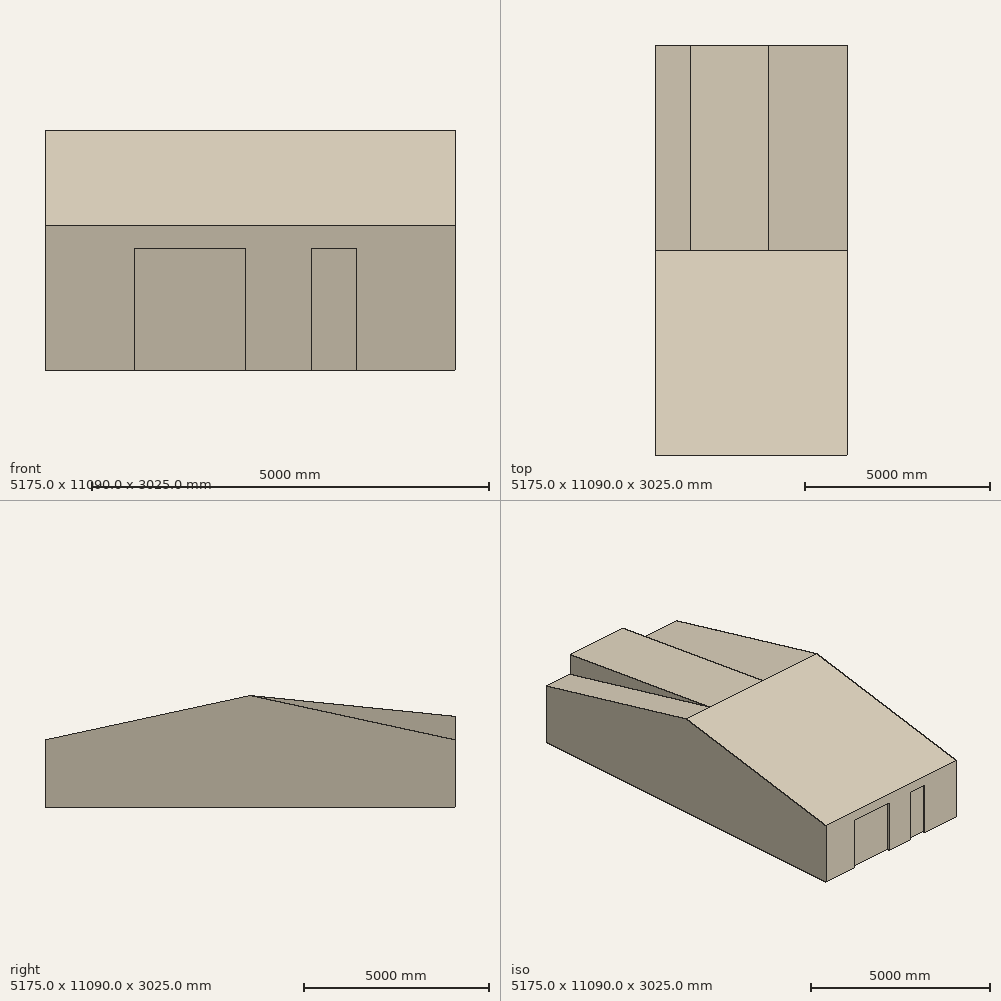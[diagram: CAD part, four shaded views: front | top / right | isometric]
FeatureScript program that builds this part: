
annotation { "Feature Type Name" : "Feature", "Feature Type Description" : "" }
export const myFeature = defineFeature(function(context is Context, id is Id, definition is map)
    precondition{}
    {
        {
            var Q0;
            Q0=qCreatedBy(makeId("Top.planeOp"),FACE);
            var sketch = newSketch(context, id + "F0", { "sketchPlane" : qUnion([Q0])});
            skLineSegment(sketch, "E0", {"start": v(0, 0) * mm, "end": v(5175, 0) * mm});
            skLineSegment(sketch, "E1", {"start": v(5175, 0) * mm, "end": v(5175, -11090) * mm});
            skLineSegment(sketch, "E2", {"start": v(5175, -11090) * mm, "end": v(0, -11090) * mm});
            skLineSegment(sketch, "E3", {"start": v(0, -11090) * mm, "end": v(0, 0) * mm});
            skSolve(sketch);
        }
        {
            var Q0;
            Q0 = qSketchRegion(id + "F0", true);
            extrude(context, id + "F1", {"entities" : qUnion([Q0]), "depth" : 3025 * mm, "offsetDistance" : 25 * mm});
        }
        {
            var Q0;
            Q0=makeQuery(id+"F1.opExtrude","SWEPT_FACE",FACE,{"disambiguationData":[OSD([sQuery(id+"F0.wireOp",EDGE,"E2")])]});
            var sketch = newSketch(context, id + "F2", { "sketchPlane" : qUnion([Q0])});
            skLineSegment(sketch, "E4", {"start": v(1120, 1540) * mm, "end": v(1120, 0) * mm});
            skLineSegment(sketch, "E5", {"start": v(1120, 1540) * mm, "end": v(2520, 1540) * mm});
            skLineSegment(sketch, "E6", {"start": v(2520, 1540) * mm, "end": v(2520, 0) * mm});
            skLineSegment(sketch, "E7", {"start": v(3360, 1540) * mm, "end": v(3360, 0) * mm});
            skLineSegment(sketch, "E8", {"start": v(3360, 1540) * mm, "end": v(3920, 1540) * mm});
            skLineSegment(sketch, "E9", {"start": v(3920, 1540) * mm, "end": v(3920, 0) * mm});
            skSolve(sketch);
        }
        {
            var Q0;
            Q0=makeQuery(id+"F1.opExtrude","SWEPT_FACE",FACE,{"disambiguationData":[OSD([sQuery(id+"F0.wireOp",EDGE,"E0")])]});
            var sketch = newSketch(context, id + "F3", { "sketchPlane" : qUnion([Q0])});
            skLineSegment(sketch, "E10", {"start": v(-2735, 1400) * mm, "end": v(-2735, 0) * mm});
            skLineSegment(sketch, "E11", {"start": v(-2735, 1400) * mm, "end": v(-1235, 1400) * mm});
            skLineSegment(sketch, "E12", {"start": v(-1235, 1400) * mm, "end": v(-1235, -91.11) * mm});
            skSolve(sketch);
        }
        {
            var Q0;
            Q0=makeQuery(id+"F1.opExtrude","SWEPT_FACE",FACE,{"disambiguationData":[OSD([sQuery(id+"F0.wireOp",EDGE,"E1")])]});
            var sketch = newSketch(context, id + "F4", { "sketchPlane" : qUnion([Q0])});
            skLineSegment(sketch, "E13", {"start": v(-5545, 3025) * mm, "end": v(-11090, 1825) * mm});
            skLineSegment(sketch, "E14", {"start": v(0, 1825) * mm, "end": v(-5545, 3025) * mm});
            skLineSegment(sketch, "E15", {"start": v(-11090, 1825) * mm, "end": v(-11090, 3025) * mm});
            skLineSegment(sketch, "E16", {"start": v(-11090, 3025) * mm, "end": v(-5545, 3025) * mm});
            skLineSegment(sketch, "E17", {"start": v(0, 3025) * mm, "end": v(0, 1825) * mm});
            skSolve(sketch);
        }
        {
            var Q0;
            {var subQ0=sQuery(id+"F4.wireOp",EDGE,"E14");Q0=makeQuery(id+"F4.imprint","IMPRINT",FACE,{"disambiguationData":[TD([[makeQuery(id+"F4.imprint","IMPRINT",EDGE,{"derivedFrom":subQ0}),-1.0]])]});}
            var Q1;
            Q1=makeQuery(id+"F4.imprint","IMPRINT",FACE,{"disambiguationData":[TD([[makeQuery(id+"F4.imprint","IMPRINT",EDGE,{"derivedFrom":sQuery(id+"F4.wireOp",EDGE,"E13")}),-1.0]])]});
            extrude(context, id + "F5", {"entities" : qUnion([Q0, Q1]), "operationType" : NewBodyOperationType.REMOVE, "oppositeDirection" : true, "depth" : 5175 * mm, "offsetDistance" : 25 * mm});
        }
        {
            var Q0;
            {var subQ0=sQuery(id+"F2.wireOp",EDGE,"E4");Q0=makeQuery(id+"F2.imprint","IMPRINT",FACE,{"disambiguationData":[TD([[makeQuery(id+"F2.imprint","IMPRINT",EDGE,{"derivedFrom":subQ0}),1.0]])]});}
            var Q1;
            {var subQ0=sQuery(id+"F2.wireOp",EDGE,"E7");Q1=makeQuery(id+"F2.imprint","IMPRINT",FACE,{"disambiguationData":[TD([[makeQuery(id+"F2.imprint","IMPRINT",EDGE,{"derivedFrom":subQ0}),1.0]])]});}
            extrude(context, id + "F6", {"entities" : qUnion([Q0, Q1]), "operationType" : NewBodyOperationType.REMOVE, "oppositeDirection" : true, "depth" : 70 * mm, "offsetDistance" : 25 * mm});
        }
        {
            var Q0;
            Q0 = qSketchRegion(id + "F3", true);
            var Q1;
            {var subQ0=sQuery(id+"F3.wireOp",EDGE,"E10");Q1=makeQuery(id+"F3.imprint","IMPRINT",FACE,{"disambiguationData":[TD([[makeQuery(id+"F3.imprint","IMPRINT",EDGE,{"derivedFrom":subQ0}),1.0]])]});}
            extrude(context, id + "F7", {"entities" : qUnion([Q0, Q1]), "operationType" : NewBodyOperationType.REMOVE, "oppositeDirection" : true, "depth" : 70 * mm, "offsetDistance" : 25 * mm});
        }
        {
            var Q0;
            Q0=makeQuery(id+"F1.opExtrude","SWEPT_FACE",FACE,{"disambiguationData":[OSD([sQuery(id+"F0.wireOp",EDGE,"E0")])]});
            var sketch = newSketch(context, id + "F8", { "sketchPlane" : qUnion([Q0])});
            skPoint(sketch, "E18", {"position": v(-1985, 2462) * mm});
            skPoint(sketch, "E18.positionSnap0", {"position": v(-1985, 1400) * mm});
            skLineSegment(sketch, "E19", {"start": v(-3035, 2462) * mm, "end": v(-935, 2462) * mm});
            skLineSegment(sketch, "E20", {"start": v(-3035, 2462) * mm, "end": v(-3035, 0) * mm});
            skLineSegment(sketch, "E21", {"start": v(-935, 2462) * mm, "end": v(-935, 0) * mm});
            skLineSegment(sketch, "E22", {"start": v(-3035, 1825) * mm, "end": v(-935, 1825) * mm});
            skSolve(sketch);
        }
        {
            var Q0;
            {var subQ0=sQuery(id+"F8.wireOp",EDGE,"E19");Q0=makeQuery(id+"F8.imprint","IMPRINT",FACE,{"disambiguationData":[TD([[makeQuery(id+"F8.imprint","IMPRINT",EDGE,{"derivedFrom":subQ0}),-1.0]])]});}
            extrude(context, id + "F9", {"entities" : qUnion([Q0]), "operationType" : NewBodyOperationType.ADD, "endBound" : BoundingType.UP_TO_NEXT, "oppositeDirection" : true, "depth" : 25 * mm, "offsetDistance" : 25 * mm});
        }
        {
            var Q0;
            Q0=makeQuery(id+"F9.opExtrude","SWEPT_FACE",FACE,{"disambiguationData":[OSD([sQuery(id+"F8.wireOp",EDGE,"E21")])]});
            var sketch = newSketch(context, id + "F10", { "sketchPlane" : qUnion([Q0])});
            skPoint(sketch, "E23", {"position": v(5545, 3025) * mm});
            skLineSegment(sketch, "E24", {"start": v(0, 2462) * mm, "end": v(5545, 3025) * mm});
            skLineSegment(sketch, "E25", {"start": v(0, 2462) * mm, "end": v(2943.47, 2462) * mm});
            skLineSegment(sketch, "E26", {"start": v(2943.47, 2462) * mm, "end": v(5545, 3025) * mm});
            skSolve(sketch);
        }
        {
            var Q0;
            Q0 = qSketchRegion(id + "F10", true);
            extrude(context, id + "F11", {"entities" : qUnion([Q0]), "operationType" : NewBodyOperationType.ADD, "oppositeDirection" : true, "depth" : 2100 * mm, "offsetDistance" : 25 * mm});
        }
    });
